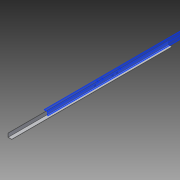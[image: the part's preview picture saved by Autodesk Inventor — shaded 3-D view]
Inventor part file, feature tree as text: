
AUTODESK INVENTOR PART (.ipt)
format: ipt  version: 2014 SP1 (Build 180222100, 222)  size: 140,288 bytes
history: native  units: in
note: dims shown in document units (in); Inventor stores cm internally (conversion verified against a paired STEP export)
features: extrude x2, sketch x2, reference x2
ambient origin geometry x8: Origin, YZ Plane, XZ Plane, XY Plane, X Axis, Y Axis, Z Axis, Center Point
bodies: Solid1 (feature_tree)
feature tree (6):
  extrude  "Extrusion1"  Depth=0.0312in
  extrude  "Extrusion2"  Depth=26.9688in TaperAngle=0.0deg
  sketch  "Sketch1"  dims[d0=0.625in d1=0.0312in]
  sketch  "Sketch2"  dims[d2=26.9688in d3=0.0in d4=1.0in d5=0.0in]
  reference  "Reference1"
  reference  "Reference2"
